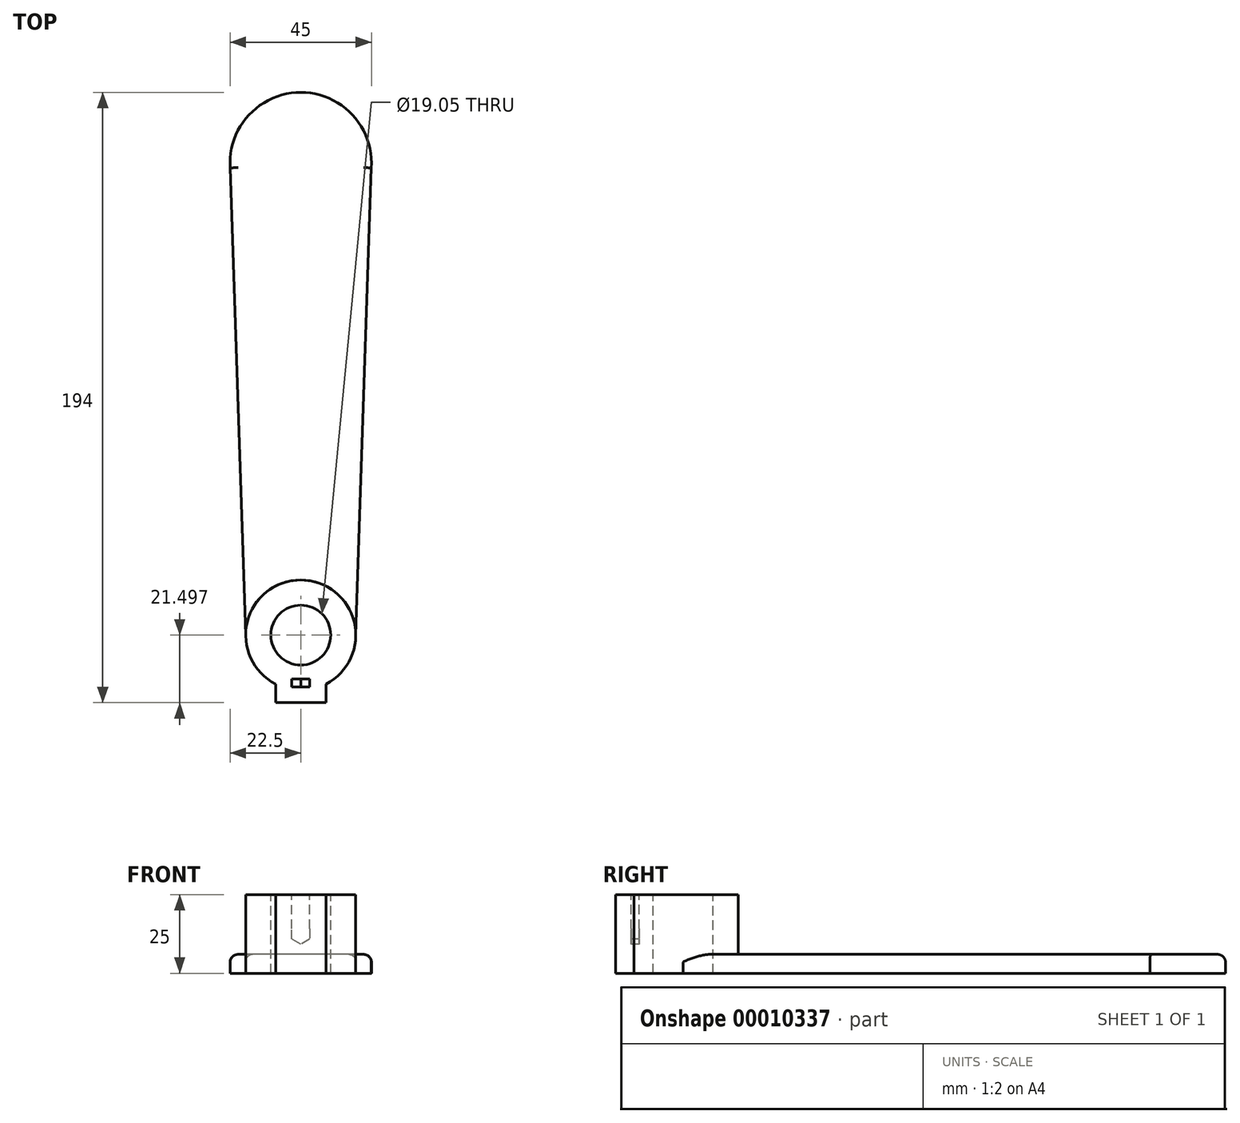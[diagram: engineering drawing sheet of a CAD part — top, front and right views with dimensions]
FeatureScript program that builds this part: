
annotation { "Feature Type Name" : "Feature", "Feature Type Description" : "" }
export const myFeature = defineFeature(function(context is Context, id is Id, definition is map)
    precondition{}
    {
        {
            var Q0;
            Q0=qCreatedBy(makeId("Top.planeOp"),FACE);
            var sketch = newSketch(context, id + "F0", { "sketchPlane" : qUnion([Q0])});
            skCircle(sketch, "E0", {"center": v(0, 123.35) * mm, "radius": 22.5 * mm});
            skCircle(sketch, "E1", {"center": v(0, -26.65) * mm, "radius": 17.5 * mm});
            skLineSegment(sketch, "E2", {"start": v(0, 123.35) * mm, "end": v(-22.5, 123.35) * mm});
            skLineSegment(sketch, "E3", {"start": v(0, -26.65) * mm, "end": v(-17.5, -26.65) * mm});
            skLineSegment(sketch, "E4", {"start": v(-17.5, -26.65) * mm, "end": v(17.5, -26.65) * mm});
            skLineSegment(sketch, "E5", {"start": v(0, 123.35) * mm, "end": v(22.5, 123.35) * mm});
            skLineSegment(sketch, "E6", {"start": v(-22.5, 123.35) * mm, "end": v(-17.5, -26.65) * mm});
            skLineSegment(sketch, "E7", {"start": v(17.5, -26.65) * mm, "end": v(22.5, 123.35) * mm});
            skLineSegment(sketch, "E8", {"start": v(-9.26, -41.5) * mm, "end": v(-9.5, -53.21) * mm});
            skLineSegment(sketch, "E9", {"start": v(-9.5, -53.21) * mm, "end": v(9.76, -53.21) * mm});
            skLineSegment(sketch, "E10", {"start": v(9.76, -53.21) * mm, "end": v(9.54, -41.65) * mm});
            skSolve(sketch);
        }
        {
            var Q0;
            Q0 = qSketchRegion(id + "F0", true);
            extrude(context, id + "F1", {"entities" : qUnion([Q0]), "depth" : 6 * mm});
        }
        {
            var Q0;
            Q0=makeQuery(id+"F1.opExtrude","CAP_EDGE",EDGE,{"disambiguationData":[OSD([sQuery(id+"F0.wireOp",EDGE,"E0")])],"isStart":false});
            var Q1;
            Q1=makeQuery(id+"F1.opExtrude","CAP_EDGE",EDGE,{"disambiguationData":[OSD([sQuery(id+"F0.wireOp",EDGE,"E7")])],"isStart":false});
            var Q2;
            Q2=makeQuery(id+"F1.opExtrude","CAP_EDGE",EDGE,{"disambiguationData":[OSD([sQuery(id+"F0.wireOp",EDGE,"E1")])],"isStart":false});
            var Q3;
            Q3=makeQuery(id+"F1.opExtrude","CAP_EDGE",EDGE,{"disambiguationData":[OSD([sQuery(id+"F0.wireOp",EDGE,"E6")])],"isStart":false});
            fillet(context, id + "F2", {"entities" : qUnion([Q0, Q1, Q2, Q3]), "radius" : 2.5 * mm, "tangentPropagation" : true, "allowEdgeOverflow" : false});
        }
        {
            var Q0;
            {var subQ0=sQuery(id+"F0.wireOp",EDGE,"E4");var subQ1=makeQuery(id+"F0.imprint","IMPRINT",VERTEX,{"derivedFrom":subQ0});Q0=makeQuery(id+"F0.imprint","IMPRINT",FACE,{"disambiguationData":[TD([[makeQuery(id+"F0.imprint","IMPRINT",EDGE,{"disambiguationData":[TD([[subQ1,1.0]])],"derivedFrom":subQ0}),-1.0]])]});}
            var Q1;
            {var subQ0=sQuery(id+"F0.wireOp",EDGE,"E4");var subQ1=makeQuery(id+"F0.imprint","IMPRINT",VERTEX,{"derivedFrom":subQ0});Q1=makeQuery(id+"F0.imprint","IMPRINT",FACE,{"disambiguationData":[TD([[makeQuery(id+"F0.imprint","IMPRINT",EDGE,{"disambiguationData":[TD([[subQ1,1.0]])],"derivedFrom":subQ0}),1.0]])]});}
            extrude(context, id + "F3", {"entities" : qUnion([Q0, Q1]), "operationType" : NewBodyOperationType.ADD, "depth" : 25 * mm});
        }
        {
            var Q0;
            Q0=makeQuery(id+"F3.opExtrude","CAP_FACE",FACE,{"disambiguationData":[OSD([sQuery(id+"F0.wireOp",EDGE,"E1")])],"isStart":false});
            var sketch = newSketch(context, id + "F4", { "sketchPlane" : qUnion([Q0])});
            skCircle(sketch, "E11", {"center": v(0, -26.65) * mm, "radius": 9.53 * mm});
            skSolve(sketch);
        }
        {
            var Q0;
            Q0 = qSketchRegion(id + "F4", true);
            extrude(context, id + "F5", {"entities" : qUnion([Q0]), "operationType" : NewBodyOperationType.REMOVE, "endBound" : BoundingType.THROUGH_ALL, "oppositeDirection" : true, "depth" : 25 * mm});
        }
        {
            var Q0;
            Q0=makeQuery(id+"F1.opExtrude","CAP_FACE",FACE,{"disambiguationData":[OSD([sQuery(id+"F0.wireOp",EDGE,"E0"),sQuery(id+"F0.wireOp",EDGE,"E1"),sQuery(id+"F0.wireOp",EDGE,"E6"),sQuery(id+"F0.wireOp",EDGE,"E7")])],"isStart":true});
            var sketch = newSketch(context, id + "F6", { "sketchPlane" : qUnion([Q0])});
            skLineSegment(sketch, "E12", {"start": v(-8, 42.22) * mm, "end": v(-8, 48.15) * mm});
            skLineSegment(sketch, "E13", {"start": v(-8, 48.15) * mm, "end": v(0, 48.15) * mm});
            skLineSegment(sketch, "E14", {"start": v(0, 48.15) * mm, "end": v(8, 48.15) * mm});
            skLineSegment(sketch, "E15", {"start": v(8, 48.15) * mm, "end": v(8, 42.22) * mm});
            skLineSegment(sketch, "E16", {"start": v(-8, 42.22) * mm, "end": v(8, 42.22) * mm});
            skSolve(sketch);
        }
        {
            var Q0;
            Q0 = qSketchRegion(id + "F6", true);
            var Q1;
            Q1=makeQuery(id+"F3.opExtrude","CAP_FACE",FACE,{"disambiguationData":[OSD([sQuery(id+"F0.wireOp",EDGE,"E1")])],"isStart":false});
            extrude(context, id + "F7", {"entities" : qUnion([Q0]), "operationType" : NewBodyOperationType.ADD, "endBound" : BoundingType.UP_TO_SURFACE, "oppositeDirection" : true, "endBoundEntityFace" : qUnion([Q1]), "depth" : 25 * mm});
        }
        {
            var Q0;
            Q0=makeQuery(id+"F7.opExtrude","SWEPT_FACE",FACE,{"disambiguationData":[OSD([sQuery(id+"F6.wireOp",EDGE,"E13"),sQuery(id+"F6.wireOp",EDGE,"E14")])]});
            cPlane(context, id + "F8", {"entities" : qUnion([Q0]), "cplaneType" : CPlaneType.OFFSET, "offset" : 5 * mm, "oppositeDirection" : true, "width" : 150 * mm, "height" : 150 * mm});
        }
        {
            var Q0;
            Q0=qCreatedBy(id+"F8.planeOp",FACE);
            var sketch = newSketch(context, id + "F9", { "sketchPlane" : qUnion([Q0])});
            skCircle(sketch, "E17.cCircle", {"center": v(0, 12.5) * mm, "radius": 2.85 * mm, "construction": true});
            skLineSegment(sketch, "E17.0", {"start": v(-2.86, 14.13) * mm, "end": v(-0.01, 15.8) * mm});
            skLineSegment(sketch, "E17.1", {"start": v(-0.01, 15.8) * mm, "end": v(2.84, 14.16) * mm});
            skLineSegment(sketch, "E17.2", {"start": v(2.84, 14.16) * mm, "end": v(2.86, 10.87) * mm});
            skLineSegment(sketch, "E17.3", {"start": v(2.86, 10.87) * mm, "end": v(0.01, 9.2) * mm});
            skLineSegment(sketch, "E17.4", {"start": v(0.01, 9.2) * mm, "end": v(-2.84, 10.84) * mm});
            skLineSegment(sketch, "E17.5", {"start": v(-2.84, 10.84) * mm, "end": v(-2.86, 14.13) * mm});
            skPoint(sketch, "E17.0.midPoint", {"position": v(-1.44, 14.96) * mm});
            skLineSegment(sketch, "E18", {"start": v(2.84, 14.16) * mm, "end": v(2.84, 25.03) * mm});
            skLineSegment(sketch, "E19", {"start": v(-2.86, 14.13) * mm, "end": v(-2.86, 25) * mm});
            skLineSegment(sketch, "E20", {"start": v(-2.86, 25) * mm, "end": v(2.84, 25.03) * mm});
            skSolve(sketch);
        }
        {
            var Q0;
            Q0 = qSketchRegion(id + "F9", true);
            extrude(context, id + "F10", {"entities" : qUnion([Q0]), "operationType" : NewBodyOperationType.REMOVE, "oppositeDirection" : true, "depth" : 2.6 * mm});
        }
    });
